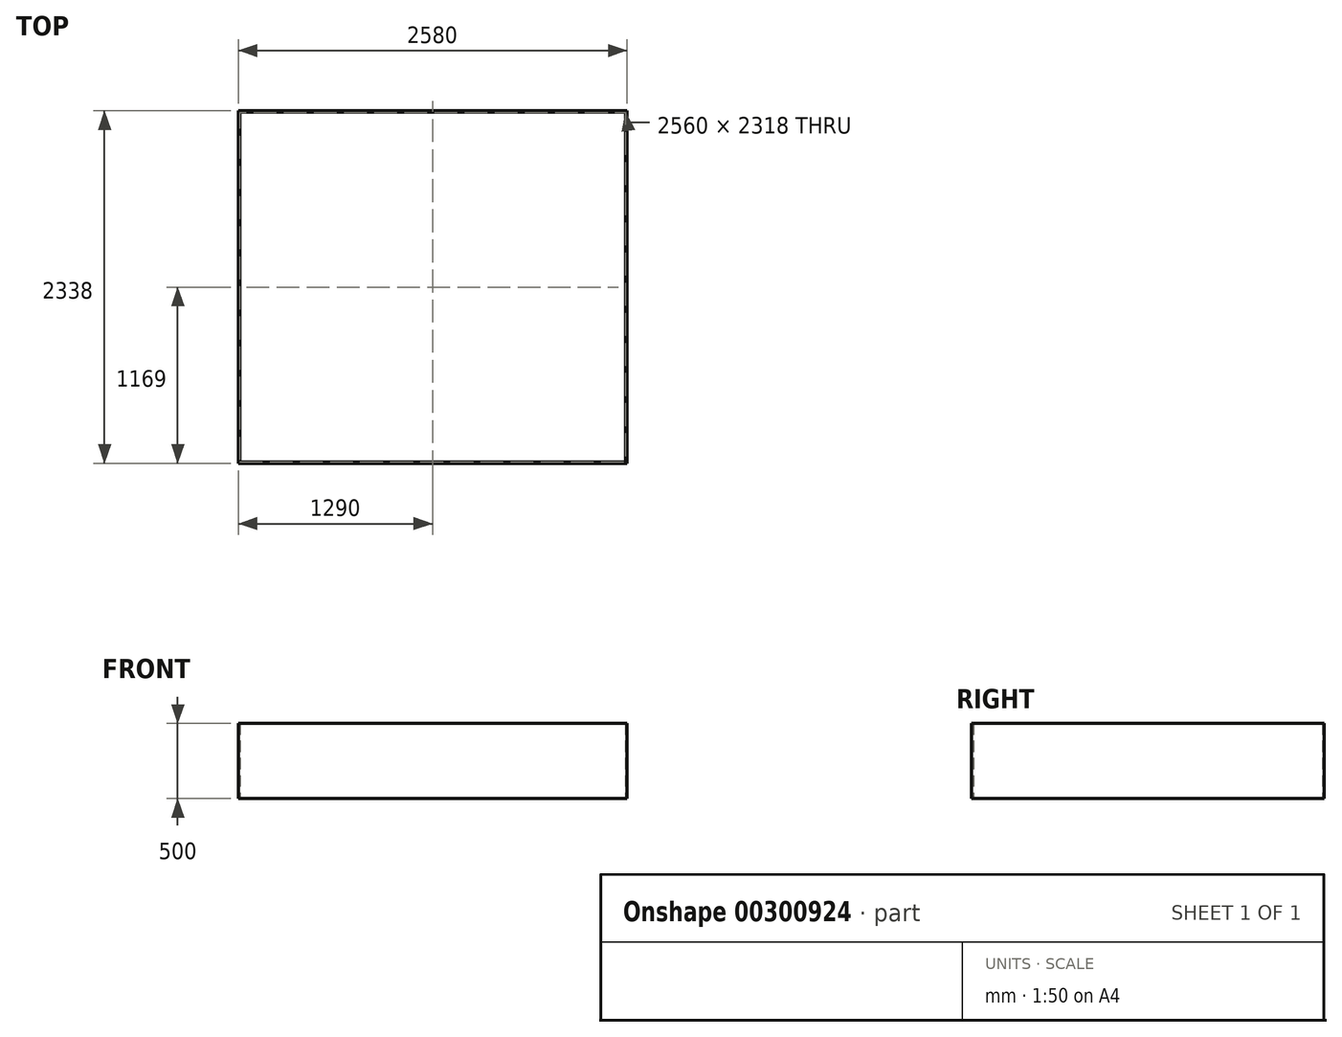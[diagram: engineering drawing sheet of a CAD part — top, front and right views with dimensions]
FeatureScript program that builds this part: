
annotation { "Feature Type Name" : "Feature", "Feature Type Description" : "" }
export const myFeature = defineFeature(function(context is Context, id is Id, definition is map)
    precondition{}
    {
        {
            var Q0;
            Q0=qCreatedBy(makeId("Top.planeOp"),FACE);
            var sketch = newSketch(context, id + "F0", { "sketchPlane" : qUnion([Q0])});
            skLineSegment(sketch, "E0.bottom", {"start": v(0, 2338) * mm, "end": v(2580, 2338) * mm});
            skLineSegment(sketch, "E0.top", {"start": v(0, 0) * mm, "end": v(2580, 0) * mm});
            skLineSegment(sketch, "E0.left", {"start": v(0, 2338) * mm, "end": v(0, 0) * mm});
            skLineSegment(sketch, "E0.right", {"start": v(2580, 2338) * mm, "end": v(2580, 0) * mm});
            skLineSegment(sketch, "E1.bottom", {"start": v(10, 2328) * mm, "end": v(2570, 2328) * mm});
            skLineSegment(sketch, "E1.top", {"start": v(10, 10) * mm, "end": v(2570, 10) * mm});
            skLineSegment(sketch, "E1.left", {"start": v(10, 2328) * mm, "end": v(10, 10) * mm});
            skLineSegment(sketch, "E1.right", {"start": v(2570, 2328) * mm, "end": v(2570, 10) * mm});
            skSolve(sketch);
        }
        {
            var Q0;
            Q0 = qSketchRegion(id + "F0", true);
            extrude(context, id + "F1", {"entities" : qUnion([Q0]), "depth" : 500 * mm});
        }
    });
